# Revit family: 61804-F-L
name_source: partatom
category: Meble
units: mm (PartAtom-declared; Revit-internal decimal feet)

## family parameters
Numer OmniClass = 23.40.20.00
Oparty na płaszczyźnie roboczej = Nie
Punkt obliczania pomieszczeń = Nie
Tnij formami wycięć po wczytaniu = Nie
Tytuł OmniClass = General Furniture and Specialties
Współdzielony = Nie
Zawsze pionowo = Tak

## types (2) — shared parameters
Hosted on larslaj.com = https://larslaj.com
Kobenhagen Materials = larslaj.com/bim
Lenght = 151 cm
Maintenance = We recommend to examine and tighten all screws and bolt clamps after a few weeks’ use. In order to prevent cracks and to extend the life of the wood, it is recommended that the wood details should be oiled every 3-5 years.
Material = Larch, stainless steel, powder coated steel
Producent = Lars Laj
Product line = Holmen
URL = https://kobenhagen.com
Width = 46 cm
metal = Kobenhagen RAL 9010
wood = Kobenhagen Wood - Larch
zero-valued in all types: Domyślna rzędna

## per-type parameters (varying)
| type | Height | Model | Opis | Product Groups | Seat height | Weight |
| 61801-f-l | 45 cm | 61801-F-L | Holmen 3-person Bench | Benches |  | 30 kg |
| 61804-f-l | 68 cm | 61804-F-L | Holmen 3-person Lounge Bench | Sofa Benches | 45 cm | 40 kg |
